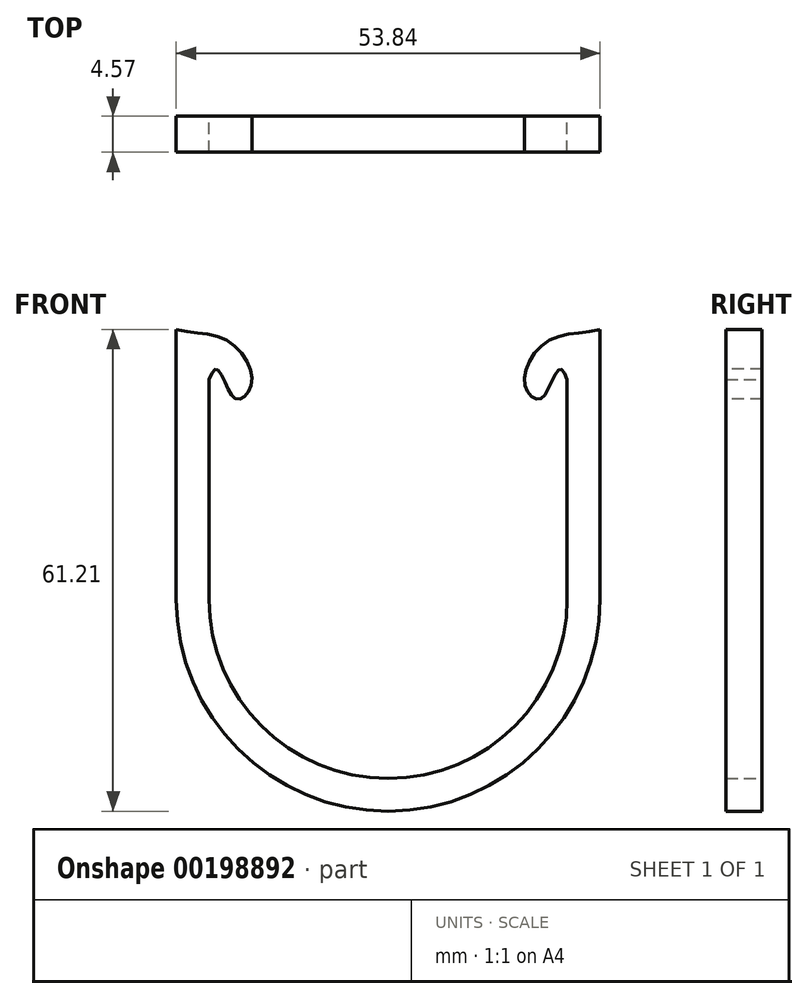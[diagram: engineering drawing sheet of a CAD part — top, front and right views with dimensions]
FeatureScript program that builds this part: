
annotation { "Feature Type Name" : "Feature", "Feature Type Description" : "" }
export const myFeature = defineFeature(function(context is Context, id is Id, definition is map)
    precondition{}
    {
        {
            var Q0;
            Q0=qCreatedBy(makeId("Front.planeOp"),FACE);
            var sketch = newSketch(context, id + "F0", { "sketchPlane" : qUnion([Q0])});
            skLineSegment(sketch, "E0", {"start": v(0, 0) * mm, "end": v(0, 34.3) * mm});
            skLineSegment(sketch, "E1", {"start": v(4.17, 27.94) * mm, "end": v(4.17, 0) * mm});
            skLineSegment(sketch, "E2", {"start": v(26.92, 68.24) * mm, "end": v(26.92, -23.55) * mm, "construction": true});
            skLineSegment(sketch, "E3.MirrorCS", {"start": v(49.67, 27.94) * mm, "end": v(49.67, 0) * mm});
            skLineSegment(sketch, "E4.MirrorCS", {"start": v(53.84, 0) * mm, "end": v(53.84, 34.3) * mm});
            skArc(sketch, "E5", {"start": v(49.67, 0) * mm, "mid": v(26.92, -22.75) * mm, "end": v(4.17, 0) * mm});
            skArc(sketch, "E6", {"start": v(53.84, 0) * mm, "mid": v(26.92, -26.92) * mm, "end": v(0, 0) * mm});
            skFitSpline(sketch, "E7", {"points": [v(0, 34.3) * mm, v(6.17, 33.05) * mm, v(9.49, 28.94) * mm, v(9.01, 26.1) * mm, v(7.59, 25.46) * mm, v(6.32, 27.36) * mm, v(5.06, 29.25) * mm, v(4.17, 27.94) * mm], "startDerivative": vector(31, -8.1) * mm, "endDerivative": vector(-8.7, -20.5) * mm});
            skFitSpline(sketch, "E8.MirrorCS", {"points": [v(53.84, 34.3) * mm, v(47.67, 33.05) * mm, v(44.35, 28.94) * mm, v(44.83, 26.1) * mm, v(46.25, 25.46) * mm, v(47.51, 27.36) * mm, v(48.78, 29.25) * mm, v(49.67, 27.94) * mm], "startDerivative": vector(-31, -8.1) * mm, "endDerivative": vector(8.7, -20.5) * mm});
            skSolve(sketch);
        }
        {
            var Q0;
            Q0 = qSketchRegion(id + "F0", true);
            extrude(context, id + "F1", {"entities" : qUnion([Q0]), "depth" : 4.57 * mm});
        }
    });
